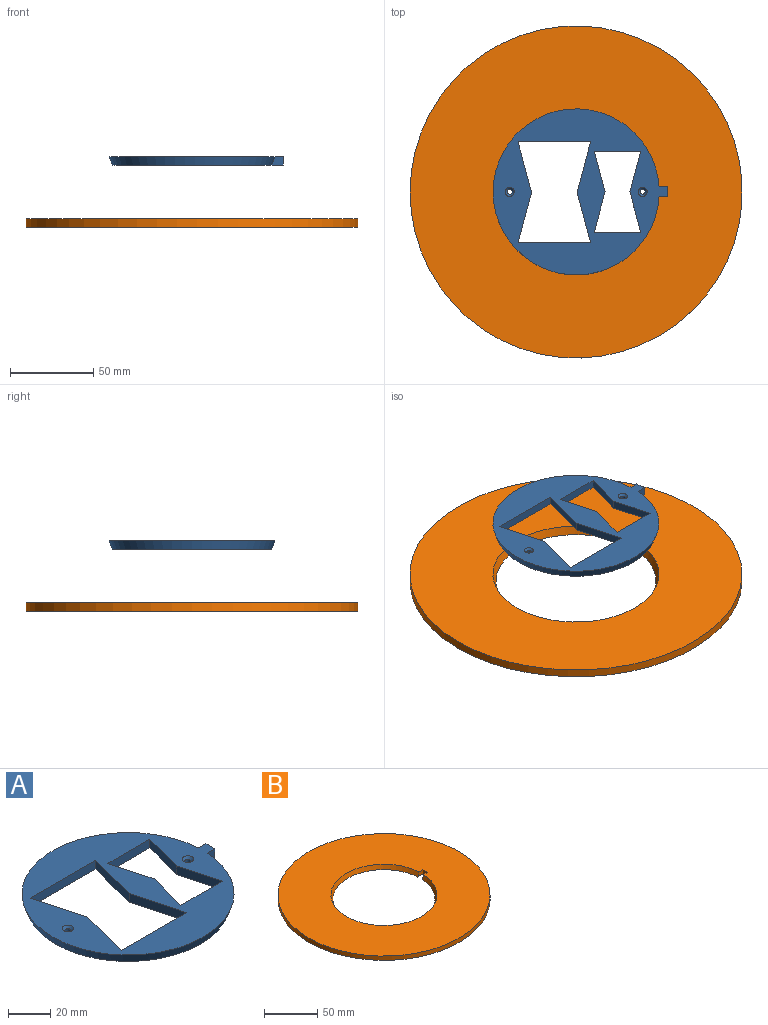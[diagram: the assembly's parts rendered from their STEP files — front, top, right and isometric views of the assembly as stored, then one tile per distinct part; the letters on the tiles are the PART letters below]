
ASSEMBLY  parts=2 mates=1
PART A: 32 faces, bbox 105x100x5 mm
  f0: plane 103.18x96.36mm, normal (0,0,-1), area 4079.9mm2, adj f4,f5,f6,f7,f8,f9,f10,f11
  f1: cylinder r=1.5mm len=3mm, axis (0,0,1), area 21.2mm2, adj f20,f31
  f2: cylinder r=1.5mm len=3mm, axis (0,0,1), area 21.2mm2, adj f21,f26
  f3: plane 105x100mm, normal (0,0,1), area 4643.3mm2, adj f4,f5,f6,f7,f8,f9,f10,f11
  f4: cone r=48.18mm half-angle=20deg, axis (0,0,1), area 1609.2mm2, adj f0,f3,f17,f18
  f5: plane 24.26x6.5mm, normal (0.97,0.26,0), area 125.6mm2, adj f0,f3,f6,f10
  f6: plane 24.26x6.5mm, normal (0.97,-0.26,0), area 125.6mm2, adj f0,f3,f5,f7
  f7: plane 28x5mm, normal (0,1,0), area 140mm2, adj f0,f3,f6,f8
  f8: plane 24.26x6.5mm, normal (-0.97,-0.26,0), area 125.6mm2, adj f0,f3,f7,f9
  f9: plane 24.26x6.5mm, normal (-0.97,0.26,0), area 125.6mm2, adj f0,f3,f8,f10
  f10: plane 28x5mm, normal (0,-1,0), area 140mm2, adj f0,f3,f5,f9
  f11: plane 30.26x8.11mm, normal (-0.97,0.26,0), area 156.6mm2, adj f0,f3,f12,f16
  f12: plane 43.64x5mm, normal (0,-1,0), area 218.2mm2, adj f0,f3,f11,f13
  f13: plane 30.26x8.11mm, normal (0.97,0.26,0), area 156.6mm2, adj f0,f3,f12,f14
  f14: plane 30.26x8.11mm, normal (0.97,-0.26,0), area 156.6mm2, adj f0,f3,f13,f15
  f15: plane 43.64x5mm, normal (0,1,0), area 218.2mm2, adj f0,f3,f14,f16
  f16: plane 30.26x8.11mm, normal (-0.97,-0.26,0), area 156.6mm2, adj f0,f3,f11,f15
  f17: plane 6.92x5mm, normal (0,-1,0), area 30mm2, adj f0,f3,f4,f19
  f18: plane 6.92x5mm, normal (0,1,0), area 30mm2, adj f0,f3,f4,f19
  f19: plane 6x5mm, normal (1,0,0), area 30mm2, adj f0,f3,f17,f18
  f20: cone r=1.5mm half-angle=45deg, axis (0,0,1), area 23.6mm2, adj f1,f3
  f21: cone r=1.5mm half-angle=45deg, axis (0,0,1), area 23.6mm2, adj f2,f3
  f22: plane 5.5x1.5mm, normal (0,1,0), area 8.3mm2, adj f0,f23,f25,f26
  f23: plane 5.5x1.5mm, normal (1,0,0), area 8.3mm2, adj f0,f22,f24,f26
  f24: plane 5.5x1.5mm, normal (0,-1,0), area 8.3mm2, adj f0,f23,f25,f26
  f25: plane 5.5x1.5mm, normal (-1,0,0), area 8.3mm2, adj f0,f22,f24,f26
  f26: plane 5.5x5.5mm, normal (0,0,-1), area 23.2mm2, adj f2,f22,f23,f24,f25
  f27: plane 5.5x1.5mm, normal (0,1,0), area 8.3mm2, adj f0,f28,f30,f31
  f28: plane 5.5x1.5mm, normal (1,0,0), area 8.3mm2, adj f0,f27,f29,f31
  f29: plane 5.5x1.5mm, normal (0,-1,0), area 8.3mm2, adj f0,f28,f30,f31
  f30: plane 5.5x1.5mm, normal (-1,0,0), area 8.3mm2, adj f0,f27,f29,f31
  f31: plane 5.5x5.5mm, normal (0,0,-1), area 23.2mm2, adj f1,f27,f28,f29,f30
PART B: 7 faces, bbox 200x200x5 mm
  f0: cone r=50mm half-angle=20deg, axis (0,0,1), area 1609.2mm2, adj f1,f3,f4,f5
  f1: plane 200x200mm, normal (0,0,1), area 23531.8mm2, adj f0,f2,f4,f5,f6
  f2: cylinder r=100mm len=200mm, axis (0,0,-1), area 3141.6mm2, adj f1,f3
  f3: plane 200x200mm, normal (0,0,-1), area 24082.2mm2, adj f0,f2,f4,f5,f6
  f4: plane 6.92x5mm, normal (0,-1,0), area 30mm2, adj f0,f1,f3,f6
  f5: plane 6.92x5mm, normal (0,1,0), area 30mm2, adj f0,f1,f3,f6
  f6: plane 6x5mm, normal (-1,0,0), area 30mm2, adj f1,f3,f4,f5
PLACE A t=(-36.76,3.69,34.86)mm
PLACE B t=(-36.76,3.69,-2.64)mm
MATE cylindrical A.f4 <-> B.f0  axis (0,0,1) through (-36.76,3.69,37.36)mm
